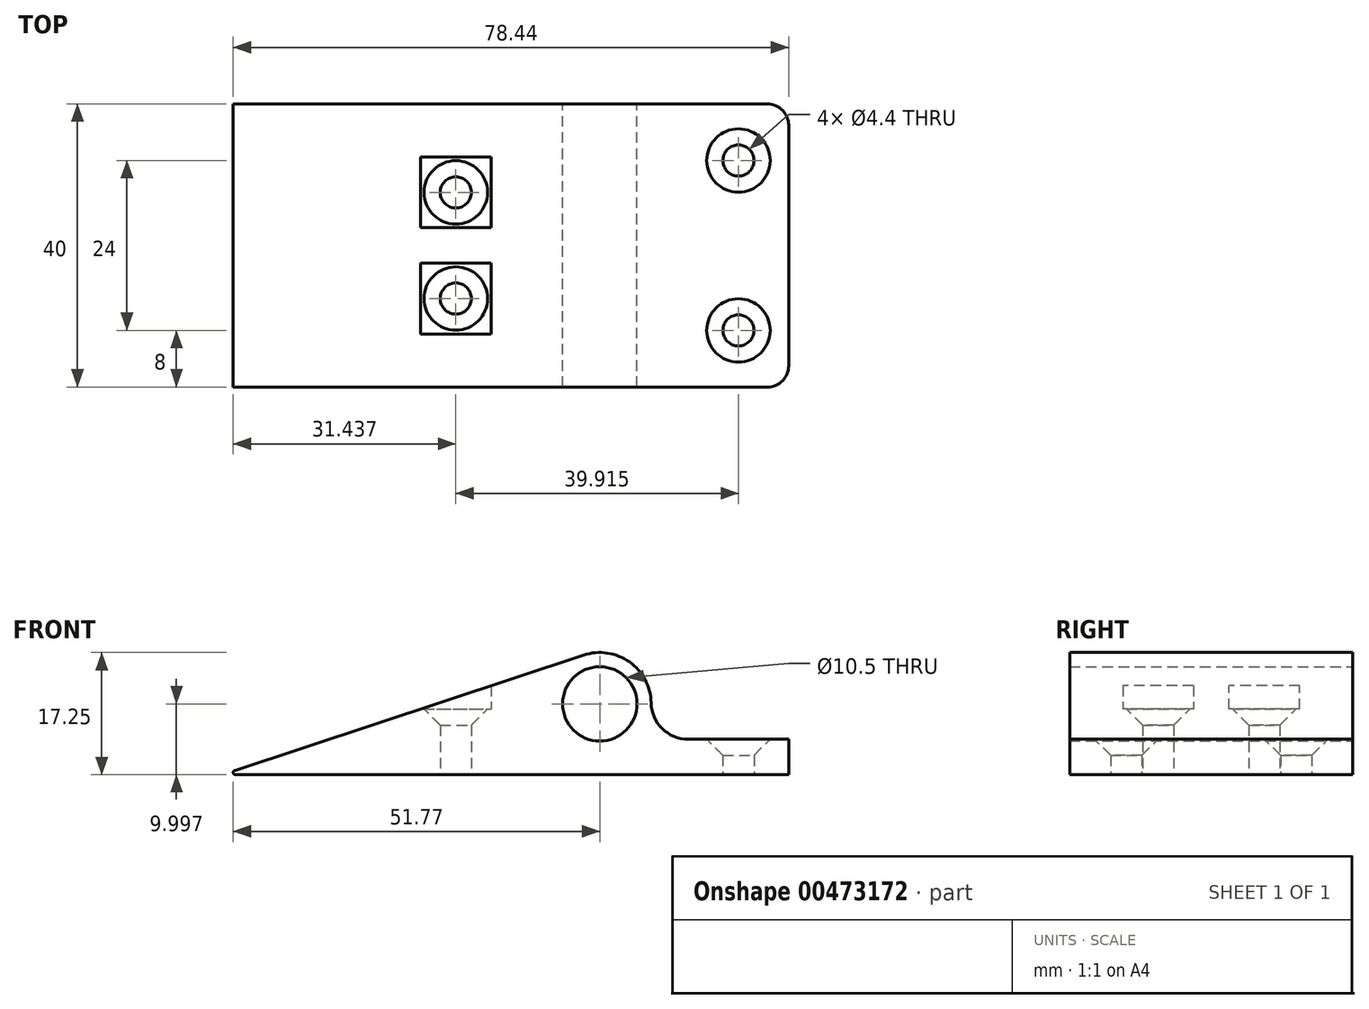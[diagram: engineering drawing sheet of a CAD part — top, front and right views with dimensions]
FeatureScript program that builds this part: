
annotation { "Feature Type Name" : "Feature", "Feature Type Description" : "" }
export const myFeature = defineFeature(function(context is Context, id is Id, definition is map)
    precondition{}
    {
        {
            assignVariable(context, id + "F0", {"name" : "Longueur_AP", "anyValue" : 40});
        }
        {
            assignVariable(context, id + "F1", {"name" : "Trou_Pivot2", "anyValue" : 10.5});
        }
        {
            var Q0;
            Q0=qCreatedBy(makeId("Front.planeOp"),FACE);
            var sketch = newSketch(context, id + "F2", { "sketchPlane" : qUnion([Q0])});
            skLineSegment(sketch, "E0.right", {"start": v(26.67, 2.36) * mm, "end": v(26.67, -2.64) * mm});
            skPoint(sketch, "E0.middle", {"position": v(0, 0) * mm});
            skCircle(sketch, "E1", {"center": v(0, 7.36) * mm, "radius": 5.25 * mm});
            skPoint(sketch, "E2", {"position": v(0, 2.36) * mm});
            skCircle(sketch, "E3", {"center": v(0, 7.36) * mm, "radius": 7.25 * mm});
            skLineSegment(sketch, "E4", {"start": v(26.67, -2.64) * mm, "end": v(-53.33, -2.64) * mm});
            skLineSegment(sketch, "E5", {"start": v(0, 2.36) * mm, "end": v(26.67, 2.36) * mm});
            skLineSegment(sketch, "E6", {"start": v(0, 2.36) * mm, "end": v(0, 7.36) * mm});
            skLineSegment(sketch, "E7", {"start": v(7.25, 7.36) * mm, "end": v(7.25, 2.36) * mm});
            skLineSegment(sketch, "E8", {"start": v(-53.33, -2.64) * mm, "end": v(-2.28, 14.24) * mm});
            skLineSegment(sketch, "E9", {"start": v(-25.33, -2.64) * mm, "end": v(-25.33, 6.62) * mm});
            skLineSegment(sketch, "E10", {"start": v(-25.33, 6.62) * mm, "end": v(-15.33, 6.62) * mm});
            skLineSegment(sketch, "E11", {"start": v(-15.33, 9.92) * mm, "end": v(-15.33, 6.62) * mm});
            skSolve(sketch);
        }
        {
            var Q0;
            Q0=makeQuery(id+"F2.imprint","IMPRINT",FACE,{"disambiguationData":[TD([[makeQuery(id+"F2.imprint","IMPRINT",EDGE,{"derivedFrom":sQuery(id+"F2.wireOp",EDGE,"E1")}),-1.0]])]});
            var Q1;
            {var subQ5=sQuery(id+"F2.wireOp",EDGE,"E0.right");Q1=makeQuery(id+"F2.imprint","IMPRINT",FACE,{"disambiguationData":[TD([[makeQuery(id+"F2.imprint","IMPRINT",EDGE,{"derivedFrom":subQ5}),-1.0]])]});}
            var Q2;
            {var subQ3=sQuery(id+"F2.wireOp",EDGE,"E9");Q2=makeQuery(id+"F2.imprint","IMPRINT",FACE,{"disambiguationData":[TD([[makeQuery(id+"F2.imprint","IMPRINT",EDGE,{"derivedFrom":subQ3}),1.0]])]});}
            var Q3;
            {var subQ0=sQuery(id+"F2.wireOp",EDGE,"E10");Q3=makeQuery(id+"F2.imprint","IMPRINT",FACE,{"disambiguationData":[TD([[makeQuery(id+"F2.imprint","IMPRINT",EDGE,{"derivedFrom":subQ0}),1.0]])]});}
            extrude(context, id + "F3", {"entities" : qUnion([Q0, Q1, Q2, Q3]), "depth" : (getVariable(context, 'Longueur_AP')) * mm, "offsetDistance" : 25 * mm, "symmetric" : true});
        }
        {
            var Q0;
            Q0=makeQuery(id+"F3.opExtrude","SWEPT_EDGE",EDGE,{"disambiguationData":[OSD([sQuery(id+"F2.wireOp",EDGE,"E3"),sQuery(id+"F2.wireOp",EDGE,"E5")])]});
            fillet(context, id + "F4", {"entities" : qUnion([Q0]), "radius" : (getVariable(context, 'Trou_Pivot2') / 2) * mm, "tangentPropagation" : true, "allowEdgeOverflow" : false});
        }
        {
            var Q0;
            Q0=makeQuery(id+"F3.opExtrude","SWEPT_EDGE",EDGE,{"disambiguationData":[OSD([sQuery(id+"F2.wireOp",EDGE,"E4"),sQuery(id+"F2.wireOp",EDGE,"E8")])]});
            fillet(context, id + "F5", {"entities" : qUnion([Q0]), "radius" : .3 * mm, "tangentPropagation" : true, "allowEdgeOverflow" : false});
        }
        {
            var Q0;
            Q0=makeQuery(id+"F3.opExtrude","SWEPT_FACE",FACE,{"disambiguationData":[OSD([sQuery(id+"F2.wireOp",EDGE,"E5")])]});
            var sketch = newSketch(context, id + "F6", { "sketchPlane" : qUnion([Q0])});
            skLineSegment(sketch, "E12", {"start": v(12.5, 12) * mm, "end": v(26.67, 12) * mm});
            skPoint(sketch, "E13", {"position": v(19.58, 12) * mm});
            skLineSegment(sketch, "E14", {"start": v(19.58, 12) * mm, "end": v(19.58, 20) * mm});
            skPoint(sketch, "E15.MirrorP", {"position": v(19.58, -12) * mm});
            skSolve(sketch);
        }
        {
            var Q0;
            Q0=sQuery(id+"F6.wireOp",VERTEX,"E13");
            var Q1;
            Q1=sQuery(id+"F6.wireOp",VERTEX,"E15.MirrorP");
            var Q2;
            Q2=makeQuery(id+"F3.opExtrude","SWEPT_BODY",BODY,{"disambiguationData":[OSD([sQuery(id+"F2.wireOp",EDGE,"E0.right"),sQuery(id+"F2.wireOp",EDGE,"E1"),sQuery(id+"F2.wireOp",EDGE,"E3"),sQuery(id+"F2.wireOp",EDGE,"E4"),sQuery(id+"F2.wireOp",EDGE,"E5"),sQuery(id+"F2.wireOp",EDGE,"E8")])]});
            hole(context, id + "F7", {"style" : HoleStyle.C_SINK, "endStyle" : HoleEndStyle.THROUGH, "standardTappedOrClearance" : lookupTablePath({ "standard" : "ISO", "fit" : "Normal", "size" : "M4", "type" : "Clearance" }), "standardBlindInLast" : lookupTablePath({ "fit" : "Standard", "standard" : "ISO", "size" : "M4", "type" : "Clearance" }), "holeDiameter" : 4.4 * mm, "cSinkDiameter" : 8.96 * mm, "cSinkAngle" : 90 * degree, "majorDiameter" : 5 * mm, "isTappedThrough" : true, "tappedDepth" : 12 * mm, "tapClearance" : 3, "locations" : qUnion([Q0, Q1]), "scope" : qUnion([Q2])});
        }
        {
            var Q0;
            {var subQ0=sQuery(id+"F2.wireOp",EDGE,"E10");Q0=makeQuery(id+"F2.imprint","IMPRINT",FACE,{"disambiguationData":[TD([[makeQuery(id+"F2.imprint","IMPRINT",EDGE,{"derivedFrom":subQ0}),1.0]])]});}
            extrude(context, id + "F8", {"entities" : qUnion([Q0]), "operationType" : NewBodyOperationType.REMOVE, "oppositeDirection" : true, "depth" : 25 * mm, "offsetDistance" : 25 * mm, "symmetric" : true});
        }
        {
            var Q0;
            Q0=makeQuery(id+"F8.boolean.opBoolean","COPY",FACE,{"derivedFrom":makeQuery(id+"F8.opExtrude","SWEPT_FACE",FACE,{"disambiguationData":[OSD([sQuery(id+"F2.wireOp",EDGE,"E10")])]})});
            var sketch = newSketch(context, id + "F9", { "sketchPlane" : qUnion([Q0])});
            skLineSegment(sketch, "E16.bottom", {"start": v(-15.33, 12.5) * mm, "end": v(-25.33, 12.5) * mm});
            skLineSegment(sketch, "E16.top", {"start": v(-15.33, -12.5) * mm, "end": v(-25.33, -12.5) * mm});
            skLineSegment(sketch, "E16.left", {"start": v(-15.33, 12.5) * mm, "end": v(-15.33, -12.5) * mm});
            skLineSegment(sketch, "E16.right", {"start": v(-25.33, 12.5) * mm, "end": v(-25.33, -12.5) * mm});
            skPoint(sketch, "E17", {"position": v(-15.33, 0) * mm});
            skLineSegment(sketch, "E18", {"start": v(-15.33, 0) * mm, "end": v(-15.33, 12.5) * mm});
            skPoint(sketch, "E19", {"position": v(-25.33, 7.5) * mm});
            skLineSegment(sketch, "E20", {"start": v(-25.33, 7.5) * mm, "end": v(-15.33, 7.5) * mm});
            skPoint(sketch, "E21", {"position": v(-20.33, 7.5) * mm});
            skPoint(sketch, "E22.MirrorP", {"position": v(-20.33, -7.5) * mm});
            skSolve(sketch);
        }
        {
            var Q0;
            Q0=sQuery(id+"F9.wireOp",VERTEX,"E22.MirrorP");
            var Q1;
            Q1=sQuery(id+"F9.wireOp",VERTEX,"E21");
            var Q2;
            Q2=makeQuery(id+"F3.opExtrude","SWEPT_BODY",BODY,{"disambiguationData":[OSD([sQuery(id+"F2.wireOp",EDGE,"E0.right"),sQuery(id+"F2.wireOp",EDGE,"E1"),sQuery(id+"F2.wireOp",EDGE,"E3"),sQuery(id+"F2.wireOp",EDGE,"E4"),sQuery(id+"F2.wireOp",EDGE,"E5"),sQuery(id+"F2.wireOp",EDGE,"E8")])]});
            hole(context, id + "F10", {"style" : HoleStyle.C_SINK, "endStyle" : HoleEndStyle.THROUGH, "standardTappedOrClearance" : lookupTablePath({ "standard" : "ISO", "fit" : "Normal", "size" : "M4", "type" : "Clearance" }), "standardBlindInLast" : lookupTablePath({ "fit" : "Standard", "standard" : "ISO", "size" : "M4", "type" : "Clearance" }), "holeDiameter" : 4.4 * mm, "cSinkDiameter" : 8.96 * mm, "cSinkAngle" : 90 * degree, "majorDiameter" : 5 * mm, "isTappedThrough" : true, "tappedDepth" : 12 * mm, "tapClearance" : 3, "locations" : qUnion([Q0, Q1]), "scope" : qUnion([Q2])});
        }
        {
            var Q0;
            {var subQ0=sQuery(id+"F2.wireOp",EDGE,"E10");Q0=makeQuery(id+"F2.imprint","IMPRINT",FACE,{"disambiguationData":[TD([[makeQuery(id+"F2.imprint","IMPRINT",EDGE,{"derivedFrom":subQ0}),1.0]])]});}
            extrude(context, id + "F11", {"entities" : qUnion([Q0]), "operationType" : NewBodyOperationType.ADD, "depth" : 5 * mm, "offsetDistance" : 25 * mm, "symmetric" : true});
        }
        {
            var Q0;
            Q0=makeQuery(id+"F3.opExtrude","CAP_EDGE",EDGE,{"disambiguationData":[OSD([sQuery(id+"F2.wireOp",EDGE,"E0.right")])],"isStart":false});
            var Q1;
            Q1=makeQuery(id+"F3.opExtrude","CAP_EDGE",EDGE,{"disambiguationData":[OSD([sQuery(id+"F2.wireOp",EDGE,"E0.right")])],"isStart":true});
            fillet(context, id + "F12", {"entities" : qUnion([Q0, Q1]), "radius" : 3 * mm, "tangentPropagation" : true, "allowEdgeOverflow" : false});
        }
    });
